# Revit family: See Through Shelf
name_source: partatom
category: Casework
revit_build: Autodesk Revit LT 2018 (Build: 20170223_1515(x64)
units: mm (PartAtom-declared; Revit-internal decimal feet)

## family parameters
Always vertical = Yes
Cut with Voids When Loaded = No
OmniClass Number = 23.40.35.00
OmniClass Title = Casework
Room Calculation Point = No
Shared = No
Work Plane-Based = Yes

## types (8) — shared parameters
Adjustable Shelves = Yes
Base Divider Panel = No
Base Full Panel = Yes
Carcase Back Thickness = 0.787 "
Carcase Material = <By Category>
Carcase Thickness = 0.787 "
Default Elevation = 48 "
Front Panel Material = <By Category>
Furniture Material = <By Category>
Handle Centred on Panel Width = No
Handle Vertical = No
Kickplate Material = <By Category>
No Base Panel = No
No Kickplate = No
No Top Panel = No
Panel Side Tolerance = 0.039 "
Shelf Material = <By Category>
Side I End Panel Extend Down = No
Side II End Panel Extend Down = No
Swing Angle = 0.00°
Top Divider Panel = No
Top Full Panel = No
Top Panel as Rails = Yes
rwcalc_Kickplate On = Yes
rwcalc_Panel Thk Base = 0.787 "
rwcalc_Panel Thk Top = 0.787 "
rwcalc_Real Panel Base Thk = 0.787 "
rwcalc_Real Panel Top Thk = 0.787 "
rwcalc_Shelf3 = No
rwcalc_Shelf4 = No
rwcalc_Shelf5 = No
rwcalc_Shelf6 = No
rwcalc_Swappable = 1
zero-valued in all types: Panel Base Extension

## per-type parameters (varying)
- UB 34.5"h x 24"d - Fixed Panel: Bottom Shelf Height=19 "; Carcase Depth=23.25 "; Carcase Height=30.5 "; Carcase Offset off Base=4 "; Construction Type=Tall; Depth=24 "; Fixed Panel=Yes; Front Panel Thickness=0.75 "; Handle Height off Base=32.125 "; Handle Horizontal=No; Handle Offset off Panel Top=2 "; Handle Offset off Side=2 "; Height=34.5 "; Inset Panel=No; Kickplate Setback=3 "; NO OF SHELVES=0; No Front Panel=No; Overlay Panel=Yes; Panel Top Tolerance=0.375 "; Shelf Thickness=1 "; Shelf to Shelf Height=10 "; Side Swing Panel=No; Single Panel=Yes; Top Rail Width=2.5 "; rwcalc_Cupboard1 Height=30.5 "; rwcalc_Front Panel Visibility=0.75 "; rwcalc_Kickplate Visibility=4 "; rwcalc_Panel Back Offset=23.25 "; rwcalc_Panel Offset off Base=4 "; rwcalc_Shelf Depth=22.463 "; rwcalc_Shelf1=No; rwcalc_Shelf2=No; rwcalc_Shelf2 Height=19 "; rwcalc_Shelf3 Height=19 "; rwcalc_Shelf4 Height=19 "; rwcalc_Shelf5 Height=19 "; rwcalc_Shelf6 Height=19 "; rwcalc_Show Single Front Panel=Yes
- UB 34.5"h x 24"d - 1 Door: Bottom Shelf Height=19 "; Carcase Depth=23.25 "; Carcase Height=30.5 "; Carcase Offset off Base=4 "; Construction Type=Tall; Depth=24 "; Fixed Panel=No; Front Panel Thickness=0.75 "; Handle Height off Base=32.125 "; Handle Horizontal=Yes; Handle Offset off Panel Top=2 "; Handle Offset off Side=2 "; Height=34.5 "; Inset Panel=No; Kickplate Setback=3 "; NO OF SHELVES=0; No Front Panel=No; Overlay Panel=Yes; Panel Top Tolerance=0.375 "; Shelf Thickness=1 "; Shelf to Shelf Height=10 "; Side Swing Panel=Yes; Single Panel=Yes; Top Rail Width=2.5 "; rwcalc_Cupboard1 Height=30.5 "; rwcalc_Front Panel Visibility=0.75 "; rwcalc_Kickplate Visibility=4 "; rwcalc_Panel Back Offset=23.25 "; rwcalc_Panel Offset off Base=4 "; rwcalc_Shelf Depth=22.463 "; rwcalc_Shelf1=No; rwcalc_Shelf2=No; rwcalc_Shelf2 Height=19 "; rwcalc_Shelf3 Height=19 "; rwcalc_Shelf4 Height=19 "; rwcalc_Shelf5 Height=19 "; rwcalc_Shelf6 Height=19 "; rwcalc_Show Single Front Panel=Yes
- UB 34.5"h x 24"d - 1 Door - 2 Shelves: Bottom Shelf Height=13.78 "; Carcase Depth=23.25 "; Carcase Height=30.5 "; Carcase Offset off Base=4 "; Construction Type=Tall; Depth=24 "; Fixed Panel=No; Front Panel Thickness=0.75 "; Handle Height off Base=32.15 "; Handle Horizontal=Yes; Handle Offset off Panel Top=2 "; Handle Offset off Side=2 "; Height=34.5 "; Inset Panel=No; Kickplate Setback=3 "; NO OF SHELVES=2; No Front Panel=No; Overlay Panel=Yes; Panel Top Tolerance=0.35 "; Shelf Thickness=1 "; Shelf to Shelf Height=10 "; Side Swing Panel=Yes; Single Panel=Yes; Top Rail Width=2.5 "; rwcalc_Cupboard1 Height=30.5 "; rwcalc_Front Panel Visibility=0.75 "; rwcalc_Kickplate Visibility=4 "; rwcalc_Panel Back Offset=23.25 "; rwcalc_Panel Offset off Base=4 "; rwcalc_Shelf Depth=22.463 "; rwcalc_Shelf1=Yes; rwcalc_Shelf2=Yes; rwcalc_Shelf2 Height=23.78 "; rwcalc_Shelf3 Height=13.78 "; rwcalc_Shelf4 Height=13.78 "; rwcalc_Shelf5 Height=13.78 "; rwcalc_Shelf6 Height=13.78 "; rwcalc_Show Single Front Panel=Yes
- UB 34.5"h x 24"d - 1 Door - 1 Shelf: Bottom Shelf Height=19 "; Carcase Depth=23.25 "; Carcase Height=30.5 "; Carcase Offset off Base=4 "; Construction Type=Tall; Depth=24 "; Fixed Panel=No; Front Panel Thickness=0.75 "; Handle Height off Base=32.125 "; Handle Horizontal=Yes; Handle Offset off Panel Top=2 "; Handle Offset off Side=2 "; Height=34.5 "; Inset Panel=No; Kickplate Setback=3 "; NO OF SHELVES=1; No Front Panel=No; Overlay Panel=Yes; Panel Top Tolerance=0.375 "; Shelf Thickness=1 "; Shelf to Shelf Height=10 "; Side Swing Panel=Yes; Single Panel=Yes; Top Rail Width=2.5 "; rwcalc_Cupboard1 Height=30.5 "; rwcalc_Front Panel Visibility=0.75 "; rwcalc_Kickplate Visibility=4 "; rwcalc_Panel Back Offset=23.25 "; rwcalc_Panel Offset off Base=4 "; rwcalc_Shelf Depth=22.463 "; rwcalc_Shelf1=Yes; rwcalc_Shelf2=No; rwcalc_Shelf2 Height=19 "; rwcalc_Shelf3 Height=19 "; rwcalc_Shelf4 Height=19 "; rwcalc_Shelf5 Height=19 "; rwcalc_Shelf6 Height=19 "; rwcalc_Show Single Front Panel=Yes
- UB 860h x 600d Inset - 1 Door - 1 Shelf: Bottom Shelf Height=18.898 "; Carcase Depth=23.622 "; Carcase Height=29.921 "; Carcase Offset off Base=3.937 "; Construction Type=Underbench; Depth=23.622 "; Fixed Panel=No; Front Panel Thickness=0.787 "; Handle Height off Base=31.496 "; Handle Horizontal=Yes; Handle Offset off Panel Top=2.323 "; Handle Offset off Side=1.969 "; Height=33.858 "; Inset Panel=Yes; Kickplate Setback=1.969 "; NO OF SHELVES=1; No Front Panel=No; Overlay Panel=No; Panel Top Tolerance=0.039 "; Shelf Thickness=0.787 "; Shelf to Shelf Height=9.843 "; Side Swing Panel=Yes; Single Panel=Yes; Top Rail Width=2.559 "; rwcalc_Cupboard1 Height=28.307 "; rwcalc_Front Panel Visibility=0.787 "; rwcalc_Kickplate Visibility=3.937 "; rwcalc_Panel Back Offset=22.835 "; rwcalc_Panel Offset off Base=4.764 "; rwcalc_Shelf Depth=22.047 "; rwcalc_Shelf1=Yes; rwcalc_Shelf2=No; rwcalc_Shelf2 Height=18.898 "; rwcalc_Shelf3 Height=18.898 "; rwcalc_Shelf4 Height=18.898 "; rwcalc_Shelf5 Height=18.898 "; rwcalc_Shelf6 Height=18.898 "; rwcalc_Show Single Front Panel=Yes
- UB 860h x 600d - Open - 2 Shelves: Bottom Shelf Height=13.78 "; Carcase Depth=22.835 "; Carcase Height=29.921 "; Carcase Offset off Base=3.937 "; Construction Type=Underbench; Depth=23.622 "; Fixed Panel=No; Front Panel Thickness=0.787 "; Handle Height off Base=31.496 "; Handle Horizontal=No; Handle Offset off Panel Top=1.969 "; Handle Offset off Side=1.969 "; Height=33.858 "; Inset Panel=No; Kickplate Setback=1.969 "; NO OF SHELVES=2; No Front Panel=Yes; Overlay Panel=Yes; Panel Top Tolerance=0.394 "; Shelf Thickness=0.787 "; Shelf to Shelf Height=9.843 "; Side Swing Panel=Yes; Single Panel=No; Top Rail Width=2.559 "; rwcalc_Cupboard1 Height=29.921 "; rwcalc_Front Panel Visibility=0.787 "; rwcalc_Kickplate Visibility=3.937 "; rwcalc_Panel Back Offset=22.835 "; rwcalc_Panel Offset off Base=3.937 "; rwcalc_Shelf Depth=22.047 "; rwcalc_Shelf1=Yes; rwcalc_Shelf2=Yes; rwcalc_Shelf2 Height=23.622 "; rwcalc_Shelf3 Height=13.78 "; rwcalc_Shelf4 Height=13.78 "; rwcalc_Shelf5 Height=13.78 "; rwcalc_Shelf6 Height=13.78 "; rwcalc_Show Single Front Panel=No
- UB 860h x 600d - Open: Bottom Shelf Height=13.78 "; Carcase Depth=22.835 "; Carcase Height=29.921 "; Carcase Offset off Base=3.937 "; Construction Type=Underbench; Depth=23.622 "; Fixed Panel=No; Front Panel Thickness=0.787 "; Handle Height off Base=31.496 "; Handle Horizontal=No; Handle Offset off Panel Top=1.969 "; Handle Offset off Side=1.969 "; Height=33.858 "; Inset Panel=No; Kickplate Setback=1.969 "; NO OF SHELVES=0; No Front Panel=Yes; Overlay Panel=Yes; Panel Top Tolerance=0.394 "; Shelf Thickness=0.787 "; Shelf to Shelf Height=9.843 "; Side Swing Panel=Yes; Single Panel=No; Top Rail Width=2.559 "; rwcalc_Cupboard1 Height=29.921 "; rwcalc_Front Panel Visibility=0.787 "; rwcalc_Kickplate Visibility=3.937 "; rwcalc_Panel Back Offset=22.835 "; rwcalc_Panel Offset off Base=3.937 "; rwcalc_Shelf Depth=22.047 "; rwcalc_Shelf1=No; rwcalc_Shelf2=No; rwcalc_Shelf2 Height=13.78 "; rwcalc_Shelf3 Height=13.78 "; rwcalc_Shelf4 Height=13.78 "; rwcalc_Shelf5 Height=13.78 "; rwcalc_Shelf6 Height=13.78 "; rwcalc_Show Single Front Panel=No
- UB 860h x 600d - Open - 1 Shelf: Bottom Shelf Height=18.898 "; Carcase Depth=22.835 "; Carcase Height=29.921 "; Carcase Offset off Base=3.937 "; Construction Type=Underbench; Depth=23.622 "; Fixed Panel=No; Front Panel Thickness=0.787 "; Handle Height off Base=31.496 "; Handle Horizontal=No; Handle Offset off Panel Top=1.969 "; Handle Offset off Side=1.969 "; Height=33.858 "; Inset Panel=No; Kickplate Setback=1.969 "; NO OF SHELVES=1; No Front Panel=Yes; Overlay Panel=Yes; Panel Top Tolerance=0.394 "; Shelf Thickness=0.787 "; Shelf to Shelf Height=9.843 "; Side Swing Panel=Yes; Single Panel=No; Top Rail Width=2.559 "; rwcalc_Cupboard1 Height=29.921 "; rwcalc_Front Panel Visibility=0.787 "; rwcalc_Kickplate Visibility=3.937 "; rwcalc_Panel Back Offset=22.835 "; rwcalc_Panel Offset off Base=3.937 "; rwcalc_Shelf Depth=22.047 "; rwcalc_Shelf1=Yes; rwcalc_Shelf2=No; rwcalc_Shelf2 Height=18.898 "; rwcalc_Shelf3 Height=18.898 "; rwcalc_Shelf4 Height=18.898 "; rwcalc_Shelf5 Height=18.898 "; rwcalc_Shelf6 Height=18.898 "; rwcalc_Show Single Front Panel=No

## geometry (parser evidence)
native form markers: Sweep x21
no freeform markers — native parametric forms only
